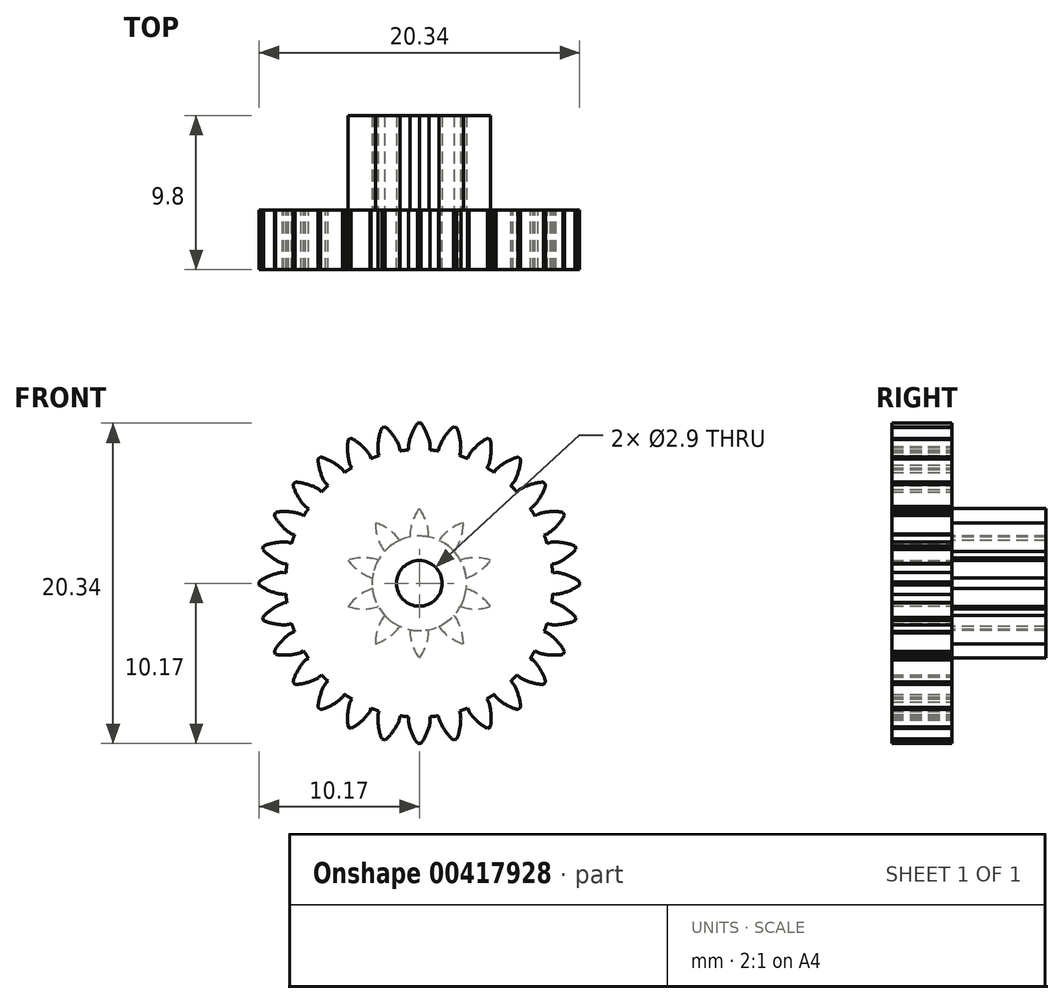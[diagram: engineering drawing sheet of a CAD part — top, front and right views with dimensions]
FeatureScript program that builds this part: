
annotation { "Feature Type Name" : "Feature", "Feature Type Description" : "" }
export const myFeature = defineFeature(function(context is Context, id is Id, definition is map)
    precondition{}
    {
        {
            var Q0;
            Q0=qCreatedBy(makeId("Front.planeOp"),FACE);
            var sketch = newSketch(context, id + "F0", { "sketchPlane" : qUnion([Q0])});
            skCircle(sketch, "E0", {"center": v(0, 0) * mm, "radius": 8.5 * mm});
            skSolve(sketch);
        }
        {
            var Q0;
            Q0=qSketchRegion(id+"F0",true);
            extrude(context, id + "F1", {"entities" : qUnion([Q0]), "depth" : 3.8 * mm});
        }
        {
            var Q0;
            Q0=qCreatedBy(makeId("Front.planeOp"),FACE);
            var sketch = newSketch(context, id + "F2", { "sketchPlane" : qUnion([Q0])});
            skLineSegment(sketch, "E1", {"start": v(0, 0) * mm, "end": v(0, -10.17) * mm, "construction": true});
            skArc(sketch, "E2.0", {"start": v(-0.67, -8.47) * mm, "mid": v(0, -8.5) * mm, "end": v(0.67, -8.47) * mm});
            skLineSegment(sketch, "E3", {"start": v(0, 0) * mm, "end": v(-0.67, -8.47) * mm, "construction": true});
            skLineSegment(sketch, "E4", {"start": v(0, 0) * mm, "end": v(0.67, -8.47) * mm, "construction": true});
            skLineSegment(sketch, "E5", {"start": v(0.67, -8.47) * mm, "end": v(0.7, -8.69) * mm});
            skFitSpline(sketch, "E6", {"points": [v(0.7, -8.69) * mm, v(0.1, -10.17) * mm], "startDerivative": vector(-0.05, -1.51) * mm, "endDerivative": vector(-0.52, -0.47) * mm});
            skLineSegment(sketch, "E7", {"start": v(0.1, -10.17) * mm, "end": v(0, -10.17) * mm});
            skLineSegment(sketch, "E8.MirrorCS", {"start": v(-0.67, -8.47) * mm, "end": v(-0.7, -8.69) * mm});
            skFitSpline(sketch, "E9.MirrorCS", {"points": [v(-0.7, -8.69) * mm, v(-0.1, -10.17) * mm], "startDerivative": vector(0.05, -1.51) * mm, "endDerivative": vector(0.52, -0.47) * mm});
            skLineSegment(sketch, "E10.MirrorCS", {"start": v(-0.1, -10.17) * mm, "end": v(0, -10.17) * mm});
            skSolve(sketch);
        }
        {
            var Q0;
            Q0 = qSketchRegion(id + "F2", true);
            var Q1;
            Q1=makeQuery(id+"F1.opExtrude","CAP_FACE",FACE,{"disambiguationData":[OSD([sQuery(id+"F0.wireOp",EDGE,"E0")])],"isStart":false});
            extrude(context, id + "F3", {"entities" : qUnion([Q0]), "endBound" : BoundingType.UP_TO_SURFACE, "endBoundEntityFace" : qUnion([Q1]), "depth" : 25 * mm});
        }
        {
            var Q0;
            Q0=qCreatedBy(makeId("Top.planeOp"),FACE);
            var sketch = newSketch(context, id + "F4", { "sketchPlane" : qUnion([Q0])});
            skLineSegment(sketch, "E11", {"start": v(0, 0) * mm, "end": v(0, 16.21) * mm, "construction": true});
            skSolve(sketch);
        }
        {
            var Q0;
            Q0=makeQuery(id+"F3.opExtrude","SWEPT_BODY",BODY,{"disambiguationData":[OSD([sQuery(id+"F2.wireOp",EDGE,"E2.0"),sQuery(id+"F2.wireOp",EDGE,"4813d95c-bd43-4883-9cd5-6db9b395fc6e"),sQuery(id+"F2.wireOp",EDGE,"a9f3b3f6-536e-4748-879d-e2f8a7a05b11")])]});
            var Q1;
            Q1=sQuery(id+"F4.wireOp",EDGE,"E11");
            circularPattern(context, id + "F5", {"operationType" : NewBodyOperationType.ADD, "entities" : qUnion([Q0]), "axis" : qUnion([Q1]), "angle" : 360 * degree, "instanceCount" : 28, "equalSpace" : true});
        }
        {
            var Q0;
            {var subQ0=makeQuery(id+"F3.opExtrude","CAP_FACE",FACE,{"disambiguationData":[OSD([sQuery(id+"F2.wireOp",EDGE,"E2.0"),sQuery(id+"F2.wireOp",EDGE,"E5"),sQuery(id+"F2.wireOp",EDGE,"E6"),sQuery(id+"F2.wireOp",EDGE,"E7"),sQuery(id+"F2.wireOp",EDGE,"E8.MirrorCS"),sQuery(id+"F2.wireOp",EDGE,"E9.MirrorCS"),sQuery(id+"F2.wireOp",EDGE,"E10.MirrorCS")])],"isStart":true});Q0=makeQuery(id+"F5.boolean.opBoolean","MERGE",FACE,{"derivedFrom":[makeQuery(id+"F1.opExtrude","CAP_FACE",FACE,{"disambiguationData":[OSD([sQuery(id+"F0.wireOp",EDGE,"E0")])],"isStart":true}),subQ0,makeQuery(id+"F5.opPattern","COPY",FACE,{"derivedFrom":subQ0,"instanceName":"1"}),makeQuery(id+"F5.opPattern","COPY",FACE,{"derivedFrom":subQ0,"instanceName":"2"}),makeQuery(id+"F5.opPattern","COPY",FACE,{"derivedFrom":subQ0,"instanceName":"3"}),makeQuery(id+"F5.opPattern","COPY",FACE,{"derivedFrom":subQ0,"instanceName":"4"}),makeQuery(id+"F5.opPattern","COPY",FACE,{"derivedFrom":subQ0,"instanceName":"5"}),makeQuery(id+"F5.opPattern","COPY",FACE,{"derivedFrom":subQ0,"instanceName":"6"}),makeQuery(id+"F5.opPattern","COPY",FACE,{"derivedFrom":subQ0,"instanceName":"7"}),makeQuery(id+"F5.opPattern","COPY",FACE,{"derivedFrom":subQ0,"instanceName":"8"}),makeQuery(id+"F5.opPattern","COPY",FACE,{"derivedFrom":subQ0,"instanceName":"9"}),makeQuery(id+"F5.opPattern","COPY",FACE,{"derivedFrom":subQ0,"instanceName":"10"}),makeQuery(id+"F5.opPattern","COPY",FACE,{"derivedFrom":subQ0,"instanceName":"11"}),makeQuery(id+"F5.opPattern","COPY",FACE,{"derivedFrom":subQ0,"instanceName":"12"}),makeQuery(id+"F5.opPattern","COPY",FACE,{"derivedFrom":subQ0,"instanceName":"13"}),makeQuery(id+"F5.opPattern","COPY",FACE,{"derivedFrom":subQ0,"instanceName":"14"}),makeQuery(id+"F5.opPattern","COPY",FACE,{"derivedFrom":subQ0,"instanceName":"15"}),makeQuery(id+"F5.opPattern","COPY",FACE,{"derivedFrom":subQ0,"instanceName":"16"}),makeQuery(id+"F5.opPattern","COPY",FACE,{"derivedFrom":subQ0,"instanceName":"17"}),makeQuery(id+"F5.opPattern","COPY",FACE,{"derivedFrom":subQ0,"instanceName":"18"}),makeQuery(id+"F5.opPattern","COPY",FACE,{"derivedFrom":subQ0,"instanceName":"19"}),makeQuery(id+"F5.opPattern","COPY",FACE,{"derivedFrom":subQ0,"instanceName":"20"}),makeQuery(id+"F5.opPattern","COPY",FACE,{"derivedFrom":subQ0,"instanceName":"21"}),makeQuery(id+"F5.opPattern","COPY",FACE,{"derivedFrom":subQ0,"instanceName":"22"}),makeQuery(id+"F5.opPattern","COPY",FACE,{"derivedFrom":subQ0,"instanceName":"23"}),makeQuery(id+"F5.opPattern","COPY",FACE,{"derivedFrom":subQ0,"instanceName":"24"}),makeQuery(id+"F5.opPattern","COPY",FACE,{"derivedFrom":subQ0,"instanceName":"25"}),makeQuery(id+"F5.opPattern","COPY",FACE,{"derivedFrom":subQ0,"instanceName":"26"}),makeQuery(id+"F5.opPattern","COPY",FACE,{"derivedFrom":subQ0,"instanceName":"27"})]});}
            var sketch = newSketch(context, id + "F6", { "sketchPlane" : qUnion([Q0])});
            skCircle(sketch, "E12", {"center": v(0, 0) * mm, "radius": 6 * mm, "construction": true});
            skCircle(sketch, "E13", {"center": v(0, 0) * mm, "radius": 1.45 * mm});
            skSolve(sketch);
        }
        {
            var Q0;
            Q0=qSketchRegion(id+"F6",true);
            extrude(context, id + "F7", {"entities" : qUnion([Q0]), "operationType" : NewBodyOperationType.REMOVE, "endBound" : BoundingType.THROUGH_ALL, "oppositeDirection" : true, "depth" : 25 * mm});
        }
        {
            var Q0;
            Q0=makeQuery(id+"F6.imprint","IMPRINT",FACE,{"disambiguationData":[TD([[makeQuery(id+"F6.imprint","IMPRINT",EDGE,{"derivedFrom":sQuery(id+"F6.wireOp",EDGE,"E13")}),-1.0]])]});
            var sketch = newSketch(context, id + "F8", { "sketchPlane" : qUnion([Q0])});
            skCircle(sketch, "E14", {"center": v(0, 0) * mm, "radius": 3 * mm});
            skLineSegment(sketch, "E15", {"start": v(0, 0) * mm, "end": v(0, 9.5) * mm, "construction": true});
            skArc(sketch, "E16", {"start": v(0, 4.75) * mm, "mid": v(-0.45, 3.9) * mm, "end": v(-0.6, 2.94) * mm});
            skLineSegment(sketch, "E17", {"start": v(-0.6, 2.94) * mm, "end": v(-0.6, -1.18) * mm, "construction": true});
            skArc(sketch, "E18.0.MirrorCS", {"start": v(0, 4.75) * mm, "mid": v(0.45, 3.9) * mm, "end": v(0.6, 2.94) * mm});
            skCircle(sketch, "E19.0", {"center": v(0, 0) * mm, "radius": 1.45 * mm});
            skSolve(sketch);
        }
        {
            var Q0;
            {var subQ1=sQuery(id+"F8.wireOp",EDGE,"E16");Q0=makeQuery(id+"F8.imprint","IMPRINT",FACE,{"disambiguationData":[TD([[makeQuery(id+"F8.imprint","IMPRINT",EDGE,{"derivedFrom":subQ1}),1.0]])]});}
            extrude(context, id + "F9", {"entities" : qUnion([Q0]), "depth" : 6 * mm});
        }
        {
            var Q0;
            Q0=makeQuery(id+"F9.opExtrude","SWEPT_BODY",BODY,{"disambiguationData":[OSD([sQuery(id+"F8.wireOp",EDGE,"E14"),sQuery(id+"F8.wireOp",EDGE,"E16"),sQuery(id+"F8.wireOp",EDGE,"E18.0.MirrorCS")])]});
            var Q1;
            Q1=sQuery(id+"F4.wireOp",EDGE,"E11");
            circularPattern(context, id + "F10", {"operationType" : NewBodyOperationType.ADD, "entities" : qUnion([Q0]), "axis" : qUnion([Q1]), "angle" : 360 * degree, "instanceCount" : 10, "equalSpace" : true});
        }
        {
            var Q0;
            Q0=qSketchRegion(id+"F8",true);
            var Q1;
            Q1=makeQuery(id+"F10.opPattern","COPY",FACE,{"derivedFrom":makeQuery(id+"F9.opExtrude","CAP_FACE",FACE,{"disambiguationData":[OSD([sQuery(id+"F8.wireOp",EDGE,"E14"),sQuery(id+"F8.wireOp",EDGE,"E16"),sQuery(id+"F8.wireOp",EDGE,"E18.0.MirrorCS")])],"isStart":false}),"instanceName":"7"});
            extrude(context, id + "F11", {"entities" : qUnion([Q0]), "endBound" : BoundingType.UP_TO_SURFACE, "endBoundEntityFace" : qUnion([Q1]), "depth" : 25 * mm});
        }
    });
